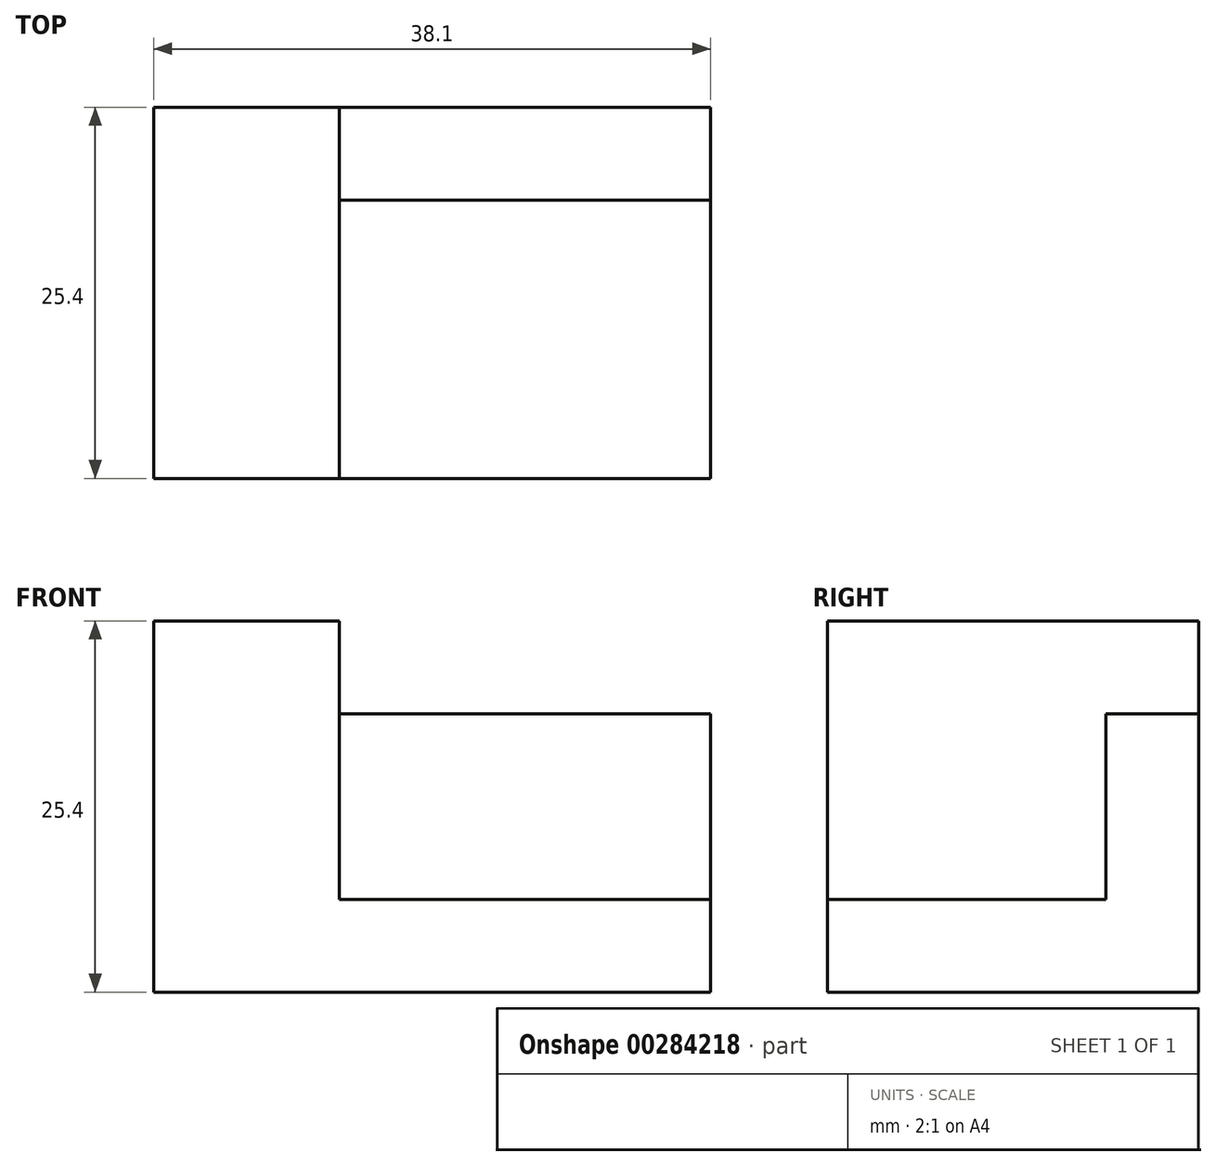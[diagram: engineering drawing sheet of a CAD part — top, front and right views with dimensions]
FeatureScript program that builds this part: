
annotation { "Feature Type Name" : "Feature", "Feature Type Description" : "" }
export const myFeature = defineFeature(function(context is Context, id is Id, definition is map)
    precondition{}
    {
        {
            var Q0;
            Q0=qCreatedBy(makeId("Front.planeOp"),FACE);
            var sketch = newSketch(context, id + "F0", { "sketchPlane" : qUnion([Q0])});
            skLineSegment(sketch, "E0", {"start": v(0, 0) * mm, "end": v(0, 25.4) * mm});
            skLineSegment(sketch, "E1", {"start": v(0, 25.4) * mm, "end": v(12.7, 25.4) * mm});
            skLineSegment(sketch, "E2", {"start": v(12.7, 25.4) * mm, "end": v(12.7, 6.35) * mm});
            skLineSegment(sketch, "E3", {"start": v(12.7, 6.35) * mm, "end": v(38.1, 6.35) * mm});
            skLineSegment(sketch, "E4", {"start": v(38.1, 6.35) * mm, "end": v(38.1, 0) * mm});
            skLineSegment(sketch, "E5", {"start": v(38.1, 0) * mm, "end": v(0, 0) * mm});
            skLineSegment(sketch, "E6", {"start": v(38.1, 6.35) * mm, "end": v(38.1, 19.05) * mm});
            skLineSegment(sketch, "E7", {"start": v(38.1, 19.05) * mm, "end": v(12.7, 19.05) * mm});
            skSolve(sketch);
        }
        {
            var Q0;
            Q0=makeQuery(id+"F0.imprint","IMPRINT",FACE,{"disambiguationData":[TD([[makeQuery(id+"F0.imprint","IMPRINT",EDGE,{"derivedFrom":sQuery(id+"F0.wireOp",EDGE,"E0")}),-1.0]])]});
            extrude(context, id + "F1", {"entities" : qUnion([Q0]), "depth" : 25.4 * mm});
        }
        {
            var Q0;
            {var subQ0=sQuery(id+"F0.wireOp",EDGE,"E3");Q0=makeQuery(id+"F0.imprint","IMPRINT",FACE,{"disambiguationData":[TD([[makeQuery(id+"F0.imprint","IMPRINT",EDGE,{"derivedFrom":subQ0}),1.0]])]});}
            extrude(context, id + "F2", {"entities" : qUnion([Q0]), "operationType" : NewBodyOperationType.ADD, "depth" : 25.4 * mm});
        }
        {
            var Q0;
            Q0=makeQuery(id+"F2.boolean.opBoolean","MERGE",FACE,{"derivedFrom":[makeQuery(id+"F1.opExtrude","SWEPT_FACE",FACE,{"disambiguationData":[OSD([sQuery(id+"F0.wireOp",EDGE,"E4")])]}),makeQuery(id+"F2.opExtrude","SWEPT_FACE",FACE,{"disambiguationData":[OSD([sQuery(id+"F0.wireOp",EDGE,"E6")])]})]});
            var sketch = newSketch(context, id + "F3", { "sketchPlane" : qUnion([Q0])});
            skLineSegment(sketch, "E8", {"start": v(0, 19.05) * mm, "end": v(-6.35, 19.05) * mm});
            skLineSegment(sketch, "E9", {"start": v(-6.35, 19.05) * mm, "end": v(-6.35, 6.35) * mm});
            skLineSegment(sketch, "E10", {"start": v(-6.35, 6.35) * mm, "end": v(-25.4, 6.35) * mm});
            skLineSegment(sketch, "E11", {"start": v(-6.35, 19.05) * mm, "end": v(-25.4, 19.05) * mm});
            skLineSegment(sketch, "E12", {"start": v(-25.4, 19.05) * mm, "end": v(-25.4, 6.35) * mm});
            skSolve(sketch);
        }
        {
            var Q0;
            Q0=makeQuery(id+"F3.imprint","IMPRINT",FACE,{"disambiguationData":[TD([[makeQuery(id+"F3.imprint","IMPRINT",EDGE,{"derivedFrom":sQuery(id+"F3.wireOp",EDGE,"E9")}),-1.0]])]});
            extrude(context, id + "F4", {"entities" : qUnion([Q0]), "operationType" : NewBodyOperationType.REMOVE, "oppositeDirection" : true, "depth" : 25.4 * mm});
        }
    });
